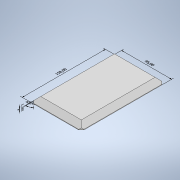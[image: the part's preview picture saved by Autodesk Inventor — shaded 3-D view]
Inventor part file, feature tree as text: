
AUTODESK INVENTOR PART (.ipt)
format: ipt  version: 2021.2 (Build 252289000, 289)  size: 137,216 bytes
history: native  units: mm
features: chamfer x8, other x6, extrude x1, sketch x1
ambient origin geometry x8: Origin, YZ Plane, XZ Plane, XY Plane, X Axis, Y Axis, Z Axis, Center Point
bodies: Body1 (feature_tree)
feature tree (16):
  other  "Твердое тело1"
  other  "Аннотации"
  extrude  "Выдавливание1"  Depth=95.0mm
  chamfer  "Фаска1"  Distance=158.0mm
  chamfer  "Фаска2"  Distance=10.0mm
  chamfer  "Фаска3"  Distance=5.0mm Angle=45.0deg
  chamfer  "Фаска4"  Distance=5.0mm Angle=45.0deg
  chamfer  "Фаска5"  Distance=5.0mm Angle=45.0deg
  chamfer  "Фаска6"  Distance=5.0mm Angle=45.0deg
  chamfer  "Фаска7"  Distance=9.0mm Angle=45.0deg
  chamfer  "Фаска8"  Distance=9.0mm Angle=45.0deg
  sketch  "Эскиз1"
  other  "Угловой размер 1"
  other  "Линейный размер 1"
  other  "Линейный размер 2"
  other  "Линейный размер 3"
